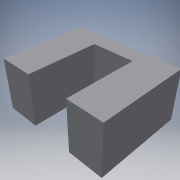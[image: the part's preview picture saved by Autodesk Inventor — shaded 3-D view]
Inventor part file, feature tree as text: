
AUTODESK INVENTOR PART (.ipt)
format: ipt  version: 2016 (Build 200138000, 138)  size: 105,472 bytes
history: native  units: in
note: dims shown in document units (in); Inventor stores cm internally (conversion verified against a paired STEP export)
features: extrude x2, sketch x2
ambient origin geometry x8: Origin, YZ Plane, XZ Plane, XY Plane, X Axis, Y Axis, Z Axis, Center Point
bodies: Solid1 (feature_tree)
feature tree (4):
  extrude  "Extrusion1"  Depth=0.2362in
  extrude  "Extrusion2"  Depth=0.1575in
  sketch  "Sketch1"  dims[d0=0.5118in d1=0.2362in]
  sketch  "Sketch2"  dims[d2=0.0787in d3=0.0in d4=0.1575in d5=0.1575in d6=0.0in d7=0.3268in d8=0.0in]
